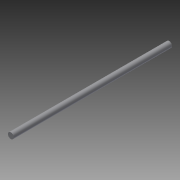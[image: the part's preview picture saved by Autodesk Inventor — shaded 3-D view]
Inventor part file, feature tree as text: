
AUTODESK INVENTOR PART (.ipt)
format: ipt  version: 2013 (Build 170138000, 138)  size: 63,488 bytes
history: native  units: in
note: dims shown in document units (in); Inventor stores cm internally (conversion verified against a paired STEP export)
features: extrude x1, sketch x1
ambient origin geometry x8: Origin, YZ Plane, XZ Plane, XY Plane, X Axis, Y Axis, Z Axis, Center Point
bodies: Solid1 (feature_tree)
feature tree (2):
  extrude  "Extrusion1"  Depth=6.75in TaperAngle=0.0deg
  sketch  "Sketch1"  dims[d1=0.25in d2=6.75in d3=0.0in]
